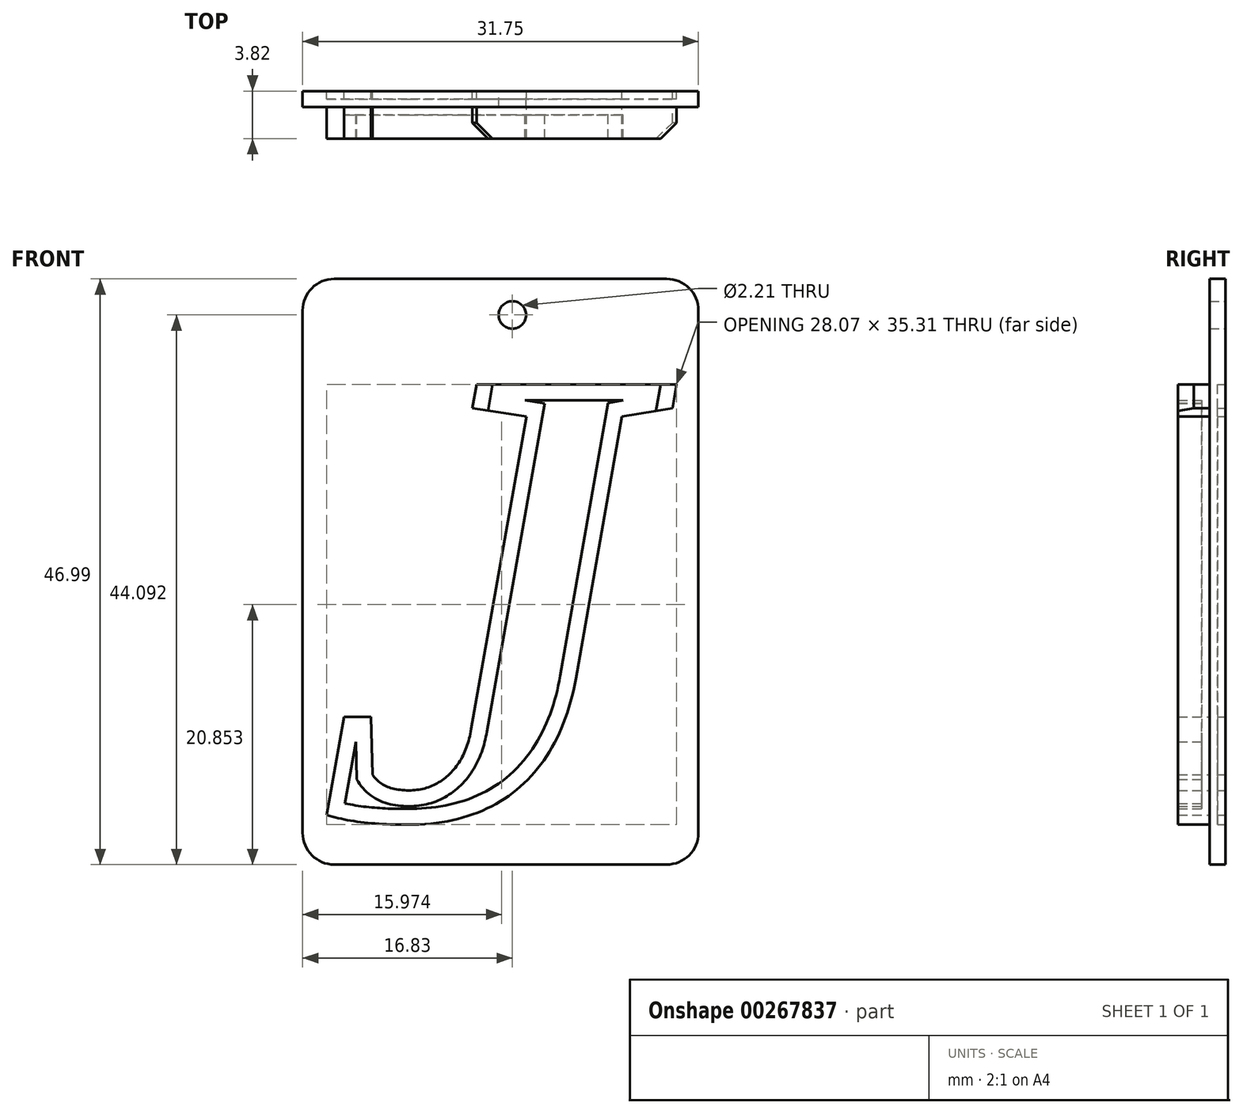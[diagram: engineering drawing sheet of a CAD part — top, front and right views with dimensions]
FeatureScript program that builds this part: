
annotation { "Feature Type Name" : "Feature", "Feature Type Description" : "" }
export const myFeature = defineFeature(function(context is Context, id is Id, definition is map)
    precondition{}
    {
        {
            var Q0;
            Q0=qCreatedBy(makeId("Front.planeOp"),FACE);
            var sketch = newSketch(context, id + "F0", { "sketchPlane" : qUnion([Q0])});
            skLineSegment(sketch, "E0.bottom", {"start": v(-33.66, 50.12) * mm, "end": v(29.84, 50.12) * mm});
            skLineSegment(sketch, "E0.left", {"start": v(-33.66, 50.12) * mm, "end": v(-33.66, -43.86) * mm});
            skLineSegment(sketch, "E0.right", {"start": v(29.84, 50.12) * mm, "end": v(29.84, -43.86) * mm});
            skLineSegment(sketch, "E1", {"start": v(-33.66, -43.86) * mm, "end": v(29.84, -43.86) * mm});
            skLineSegment(sketch, "E2.bottom", {"start": v(-31.12, 47.58) * mm, "end": v(27.3, 47.58) * mm});
            skLineSegment(sketch, "E2.top", {"start": v(-31.12, -41.32) * mm, "end": v(27.3, -41.32) * mm});
            skLineSegment(sketch, "E2.left", {"start": v(-31.12, 47.58) * mm, "end": v(-31.12, -41.32) * mm});
            skLineSegment(sketch, "E2.right", {"start": v(27.3, 47.58) * mm, "end": v(27.3, -41.32) * mm});
            skText(sketch, "E3", { "text": "J\n", "fontName": "Tinos-BoldItalic.ttf"});
            skCircle(sketch, "E4", {"center": v(0, 44.32) * mm, "radius": 2.2 * mm});
            const initialGuessF0  = {"E3": [-0.02957, -0.03642, 1, 0, 0.0765]};
            skSetInitialGuess(sketch, initialGuessF0);
            skSolve(sketch);
        }
        {
            var Q0;
            Q0=makeQuery(id+"F0.imprint","IMPRINT",FACE,{"disambiguationData":[TD([[makeQuery(id+"F0.imprint","IMPRINT",EDGE,{"derivedFrom":sQuery(id+"F0.wireOp",EDGE,"E3.sketch_text.stroke-0")}),-1.0]])]});
            extrude(context, id + "F1", {"entities" : qUnion([Q0]), "depth" : 6.35 * mm});
        }
        {
            var Q0;
            Q0=sQuery(id+"F0.wireOp",EDGE,"E0.bottom");
            var Q1;
            Q1=sQuery(id+"F0.wireOp",EDGE,"E2.bottom");
            var Q2;
            Q2=sQuery(id+"F0.wireOp",EDGE,"E2.left");
            var Q3;
            Q3=sQuery(id+"F0.wireOp",EDGE,"E0.left");
            var Q4;
            Q4=sQuery(id+"F0.wireOp",EDGE,"E1");
            var Q5;
            Q5=sQuery(id+"F0.wireOp",EDGE,"E2.top");
            var Q6;
            Q6=sQuery(id+"F0.wireOp",EDGE,"E2.right");
            var Q7;
            Q7=sQuery(id+"F0.wireOp",EDGE,"E0.right");
            extrude(context, id + "F2", {"bodyType" : ToolBodyType.SURFACE, "surfaceEntities" : qUnion([Q0, Q1, Q2, Q3, Q4, Q5, Q6, Q7]), "depth" : 6.35 * mm, "symmetric" : true});
        }
        {
            var Q0;
            Q0=makeQuery(id+"F0.imprint","IMPRINT",FACE,{"disambiguationData":[TD([[makeQuery(id+"F0.imprint","IMPRINT",EDGE,{"derivedFrom":sQuery(id+"F0.wireOp",EDGE,"E2.bottom")}),-1.0]])]});
            extrude(context, id + "F3", {"entities" : qUnion([Q0]), "operationType" : NewBodyOperationType.ADD, "depth" : 2.54 * mm, "symmetric" : true});
        }
        {
            var Q0;
            Q0=makeQuery(id+"F0.imprint","IMPRINT",FACE,{"disambiguationData":[TD([[makeQuery(id+"F0.imprint","IMPRINT",EDGE,{"derivedFrom":sQuery(id+"F0.wireOp",EDGE,"E0.bottom")}),-1.0]])]});
            extrude(context, id + "F4", {"entities" : qUnion([Q0]), "operationType" : NewBodyOperationType.ADD, "depth" : 2.54 * mm, "symmetric" : true});
        }
        {
            var Q0;
            Q0=makeQuery(id+"F2.opExtrude","SWEPT_EDGE",EDGE,{"disambiguationData":[OSD([sQuery(id+"F0.wireOp",VERTEX,"E0.left.start")])]});
            fillet(context, id + "F5", {"entities" : qUnion([Q0]), "radius" : 5.08 * mm, "tangentPropagation" : true, "allowEdgeOverflow" : false});
        }
        {
            var Q0;
            Q0=makeQuery(id+"F4.opExtrude","SWEPT_EDGE",EDGE,{"disambiguationData":[OSD([sQuery(id+"F0.wireOp",EDGE,"E0.bottom"),sQuery(id+"F0.wireOp",EDGE,"E0.left")])]});
            fillet(context, id + "F6", {"entities" : qUnion([Q0]), "radius" : 5.08 * mm, "tangentPropagation" : true, "allowEdgeOverflow" : false});
        }
        {
            var Q0;
            Q0=makeQuery(id+"F2.opExtrude","SWEPT_EDGE",EDGE,{"disambiguationData":[OSD([sQuery(id+"F0.wireOp",VERTEX,"E0.right.start")])]});
            fillet(context, id + "F7", {"entities" : qUnion([Q0]), "radius" : 5.08 * mm, "tangentPropagation" : true, "allowEdgeOverflow" : false});
        }
        {
            var Q0;
            Q0=makeQuery(id+"F2.opExtrude","SWEPT_EDGE",EDGE,{"disambiguationData":[OSD([sQuery(id+"F0.wireOp",VERTEX,"E1.start")])]});
            fillet(context, id + "F8", {"entities" : qUnion([Q0]), "radius" : 5.08 * mm, "tangentPropagation" : true, "allowEdgeOverflow" : false});
        }
        {
            var Q0;
            Q0=makeQuery(id+"F4.opExtrude","SWEPT_EDGE",EDGE,{"disambiguationData":[OSD([sQuery(id+"F0.wireOp",EDGE,"E0.left"),sQuery(id+"F0.wireOp",EDGE,"E1")])]});
            fillet(context, id + "F9", {"entities" : qUnion([Q0]), "radius" : 5.08 * mm, "tangentPropagation" : true, "allowEdgeOverflow" : false});
        }
        {
            var Q0;
            Q0=makeQuery(id+"F4.opExtrude","SWEPT_EDGE",EDGE,{"disambiguationData":[OSD([sQuery(id+"F0.wireOp",EDGE,"E0.bottom"),sQuery(id+"F0.wireOp",EDGE,"E0.right")])]});
            fillet(context, id + "F10", {"entities" : qUnion([Q0]), "radius" : 5.08 * mm, "tangentPropagation" : true, "allowEdgeOverflow" : false});
        }
        {
            var Q0;
            Q0=makeQuery(id+"F2.opExtrude","SWEPT_EDGE",EDGE,{"disambiguationData":[OSD([sQuery(id+"F0.wireOp",VERTEX,"E0.right.end")])]});
            fillet(context, id + "F11", {"entities" : qUnion([Q0]), "radius" : 5.08 * mm, "tangentPropagation" : true, "allowEdgeOverflow" : false});
        }
        {
            var Q0;
            Q0=makeQuery(id+"F4.opExtrude","SWEPT_EDGE",EDGE,{"disambiguationData":[OSD([sQuery(id+"F0.wireOp",EDGE,"E0.right"),sQuery(id+"F0.wireOp",EDGE,"E1")])]});
            fillet(context, id + "F12", {"entities" : qUnion([Q0]), "radius" : 5.08 * mm, "tangentPropagation" : true, "allowEdgeOverflow" : false});
        }
        {
            var Q0;
            Q0=makeQuery(id+"F2.opExtrude","SWEPT_FACE",FACE,{"disambiguationData":[OSD([sQuery(id+"F0.wireOp",EDGE,"E2.left")])]});
            fillet(context, id + "F13", {"entities" : qUnion([Q0]), "radius" : 5.08 * mm, "tangentPropagation" : true, "allowEdgeOverflow" : false});
        }
        {
            var Q0;
            Q0=makeQuery(id+"F2.opExtrude","SWEPT_FACE",FACE,{"disambiguationData":[OSD([sQuery(id+"F0.wireOp",EDGE,"E2.right")])]});
            fillet(context, id + "F14", {"entities" : qUnion([Q0]), "radius" : 5.08 * mm, "tangentPropagation" : true, "allowEdgeOverflow" : false});
        }
        {
            var Q0;
            Q0=makeQuery(id+"F1.opExtrude","CAP_FACE",FACE,{"disambiguationData":[OSD([sQuery(id+"F0.wireOp",EDGE,"E3.sketch_text.stroke-0"),sQuery(id+"F0.wireOp",EDGE,"E3.sketch_text.stroke-1"),sQuery(id+"F0.wireOp",EDGE,"E3.sketch_text.stroke-2"),sQuery(id+"F0.wireOp",EDGE,"E3.sketch_text.stroke-3"),sQuery(id+"F0.wireOp",EDGE,"E3.sketch_text.stroke-4"),sQuery(id+"F0.wireOp",EDGE,"E3.sketch_text.stroke-5"),sQuery(id+"F0.wireOp",EDGE,"E3.sketch_text.stroke-6"),sQuery(id+"F0.wireOp",EDGE,"E3.sketch_text.stroke-7"),sQuery(id+"F0.wireOp",EDGE,"E3.sketch_text.stroke-8"),sQuery(id+"F0.wireOp",EDGE,"E3.sketch_text.stroke-9"),sQuery(id+"F0.wireOp",EDGE,"E3.sketch_text.stroke-10"),sQuery(id+"F0.wireOp",EDGE,"E3.sketch_text.stroke-11"),sQuery(id+"F0.wireOp",EDGE,"E3.sketch_text.stroke-12"),sQuery(id+"F0.wireOp",EDGE,"E3.sketch_text.stroke-13"),sQuery(id+"F0.wireOp",EDGE,"E3.sketch_text.stroke-14"),sQuery(id+"F0.wireOp",EDGE,"E3.sketch_text.stroke-15")])],"isStart":false});
            shell(context, id + "F15", {"entities" : qUnion([Q0]), "thickness" : 2.54 * mm});
        }
        {
            var Q0;
            Q0=makeQuery(id+"F1.opExtrude","CAP_EDGE",EDGE,{"disambiguationData":[OSD([sQuery(id+"F0.wireOp",EDGE,"E3.sketch_text.stroke-1")])],"isStart":false});
            chamfer(context, id + "F16", {"entities" : qUnion([Q0]), "width" : 2.54 * mm, "tangentPropagation" : true});
        }
        {
            var Q0;
            Q0=makeQuery(id+"F1.opExtrude","CAP_EDGE",EDGE,{"disambiguationData":[OSD([sQuery(id+"F0.wireOp",EDGE,"E3.sketch_text.stroke-3")])],"isStart":false});
            chamfer(context, id + "F17", {"entities" : qUnion([Q0]), "width" : 2.54 * mm, "tangentPropagation" : true});
        }
        {
            var Q0;
            Q0=makeQuery(id+"F1.opExtrude","SWEPT_BODY",BODY,{"disambiguationData":[OSD([sQuery(id+"F0.wireOp",EDGE,"E3.sketch_text.stroke-0"),sQuery(id+"F0.wireOp",EDGE,"E3.sketch_text.stroke-1"),sQuery(id+"F0.wireOp",EDGE,"E3.sketch_text.stroke-2"),sQuery(id+"F0.wireOp",EDGE,"E3.sketch_text.stroke-3"),sQuery(id+"F0.wireOp",EDGE,"E3.sketch_text.stroke-4"),sQuery(id+"F0.wireOp",EDGE,"E3.sketch_text.stroke-5"),sQuery(id+"F0.wireOp",EDGE,"E3.sketch_text.stroke-6"),sQuery(id+"F0.wireOp",EDGE,"E3.sketch_text.stroke-7"),sQuery(id+"F0.wireOp",EDGE,"E3.sketch_text.stroke-8"),sQuery(id+"F0.wireOp",EDGE,"E3.sketch_text.stroke-9"),sQuery(id+"F0.wireOp",EDGE,"E3.sketch_text.stroke-10"),sQuery(id+"F0.wireOp",EDGE,"E3.sketch_text.stroke-11"),sQuery(id+"F0.wireOp",EDGE,"E3.sketch_text.stroke-12"),sQuery(id+"F0.wireOp",EDGE,"E3.sketch_text.stroke-13"),sQuery(id+"F0.wireOp",EDGE,"E3.sketch_text.stroke-14"),sQuery(id+"F0.wireOp",EDGE,"E3.sketch_text.stroke-15")])]});
            var Q1;
            Q1=makeQuery(id+"F2.opExtrude","SWEPT_BODY",BODY,{"disambiguationData":[OSD([sQuery(id+"F0.wireOp",EDGE,"E0.left")])]});
            var Q2;
            Q2=makeQuery(id+"F2.opExtrude","SWEPT_BODY",BODY,{"disambiguationData":[OSD([sQuery(id+"F0.wireOp",EDGE,"E2.left")])]});
            var Q3;
            Q3=qCreatedBy(makeId("Origin.pointOp"),VERTEX);
            transform(context, id + "F18", {"entities" : qUnion([Q0, Q1, Q2]), "transformType" : TransformType.SCALE_UNIFORMLY, "scale" : .5, "scalePoint" : qUnion([Q3]), "makeCopy" : false});
        }
    });
